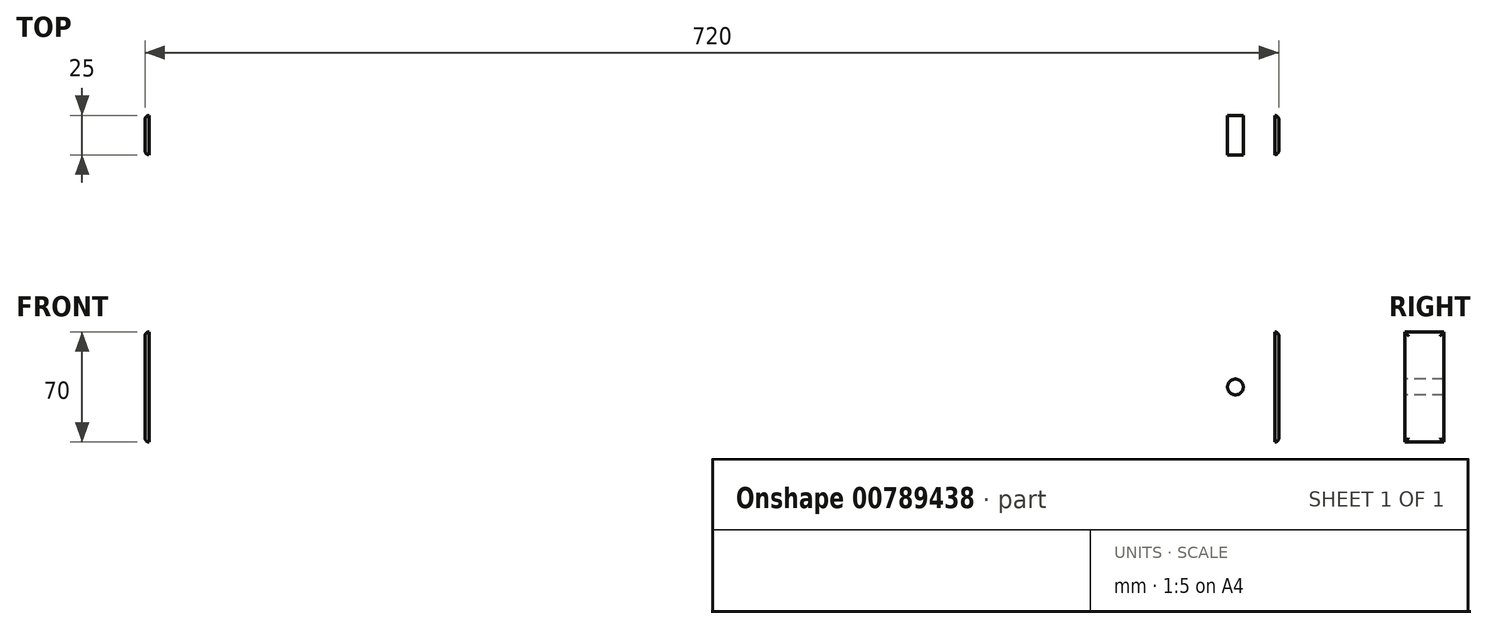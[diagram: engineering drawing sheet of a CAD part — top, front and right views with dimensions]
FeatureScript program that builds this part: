
annotation { "Feature Type Name" : "Feature", "Feature Type Description" : "" }
export const myFeature = defineFeature(function(context is Context, id is Id, definition is map)
    precondition{}
    {
        {
            var Q0;
            Q0=qCreatedBy(makeId("Right.planeOp"),FACE);
            var sketch = newSketch(context, id + "F0", { "sketchPlane" : qUnion([Q0])});
            skLineSegment(sketch, "E0.bottom", {"start": v(0, 0) * mm, "end": v(-25, 0) * mm});
            skLineSegment(sketch, "E0.top", {"start": v(0, 70) * mm, "end": v(-25, 70) * mm});
            skLineSegment(sketch, "E0.left", {"start": v(0, 0) * mm, "end": v(0, 70) * mm});
            skLineSegment(sketch, "E0.right", {"start": v(-25, 0) * mm, "end": v(-25, 70) * mm});
            skSolve(sketch);
        }
        {
            var Q0;
            Q0=makeQuery(id+"F0.imprint","IMPRINT",FACE,{"disambiguationData":[TD([[makeQuery(id+"F0.imprint","IMPRINT",EDGE,{"derivedFrom":sQuery(id+"F0.wireOp",EDGE,"E0.bottom")}),-1.0]])]});
            extrude(context, id + "F1", {"entities" : qUnion([Q0]), "oppositeDirection" : true, "depth" : 720 * mm, "offsetDistance" : 25 * mm});
        }
        {
            var Q0;
            Q0=makeQuery(id+"F1.opExtrude","CAP_FACE",FACE,{"disambiguationData":[OSD([sQuery(id+"F0.wireOp",EDGE,"E0.bottom"),sQuery(id+"F0.wireOp",EDGE,"E0.top"),sQuery(id+"F0.wireOp",EDGE,"E0.left"),sQuery(id+"F0.wireOp",EDGE,"E0.right")])],"isStart":true});
            fillet(context, id + "F2", {"entities" : qUnion([Q0]), "radius" : 2.5 * mm, "tangentPropagation" : true, "allowEdgeOverflow" : false});
        }
        {
            var Q0;
            Q0=makeQuery(id+"F1.opExtrude","CAP_FACE",FACE,{"disambiguationData":[OSD([sQuery(id+"F0.wireOp",EDGE,"E0.bottom"),sQuery(id+"F0.wireOp",EDGE,"E0.top"),sQuery(id+"F0.wireOp",EDGE,"E0.left"),sQuery(id+"F0.wireOp",EDGE,"E0.right")])],"isStart":false});
            fillet(context, id + "F3", {"entities" : qUnion([Q0]), "radius" : 2.5 * mm, "tangentPropagation" : true, "allowEdgeOverflow" : false});
        }
        {
            var Q0;
            Q0=makeQuery(id+"F1.opExtrude","SWEPT_FACE",FACE,{"disambiguationData":[OSD([sQuery(id+"F0.wireOp",EDGE,"E0.right")])]});
            var sketch = newSketch(context, id + "F4", { "sketchPlane" : qUnion([Q0])});
            skCircle(sketch, "E1", {"center": v(-692.5, 35) * mm, "radius": 5 * mm});
            skPoint(sketch, "E1.centerSnap0", {"position": v(-717.5, 35) * mm});
            skLineSegment(sketch, "E2", {"start": v(-360, 70) * mm, "end": v(-360, 142.54) * mm});
            skCircle(sketch, "E3.MirrorC", {"center": v(-27.5, 35) * mm, "radius": 5 * mm});
            skSolve(sketch);
        }
        {
            var Q0;
            Q0=makeQuery(id+"F4.imprint","IMPRINT",FACE,{"disambiguationData":[TD([[makeQuery(id+"F4.imprint","IMPRINT",EDGE,{"derivedFrom":sQuery(id+"F4.wireOp",EDGE,"E1")}),1.0]])]});
            var Q1;
            Q1=makeQuery(id+"F4.imprint","IMPRINT",FACE,{"disambiguationData":[TD([[makeQuery(id+"F4.imprint","IMPRINT",EDGE,{"derivedFrom":sQuery(id+"F4.wireOp",EDGE,"E3.MirrorC")}),-1.0]])]});
            extrude(context, id + "F5", {"entities" : qUnion([Q0, Q1]), "operationType" : NewBodyOperationType.REMOVE, "endBound" : BoundingType.THROUGH_ALL, "oppositeDirection" : true, "depth" : 25 * mm, "offsetDistance" : 25 * mm});
        }
    });
